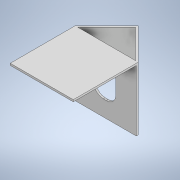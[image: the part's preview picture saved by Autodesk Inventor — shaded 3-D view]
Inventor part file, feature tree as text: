
AUTODESK INVENTOR PART (.ipt)
format: ipt  version: 2020 (Build 240168000, 168)  size: 139,776 bytes
history: native  units: mm
features: extrude x4, sketch x4
ambient origin geometry x8: Origin, YZ Plane, XZ Plane, XY Plane, X Axis, Y Axis, Z Axis, Center Point
bodies: Solid1 (feature_tree)
feature tree (8):
  extrude  "Extrusion1"  Depth=100.0mm
  extrude  "Extrusion2"  TaperAngle=45.0deg  [1 undecoded]
  extrude  "Extrusion3"  Depth=3.0mm
  extrude  "Extrusion5"  Depth=35.0mm
  sketch  "Sketch1"  dims[d0=100.0mm d1=100.0mm]
  sketch  "Sketch2"  dims[d2=3.0mm d3=0.0mm d4=45.0deg]
  sketch  "Sketch3"  dims[d5=3.0mm d6=3.0mm]
  sketch  "Sketch5"  dims[d7=55.0mm d8=0.0mm d9=35.0mm d10=50.0mm d11=15.0mm d12=3.0mm d13=0.0mm d16=100.0mm d17=100.0mm d18=3.0mm d19=0.0mm]
note: 1 required parameter value undecoded (feature->parameter linkage not recoverable at this tier; creation-order binding heuristic only, values carry confidence <= 0.55)
